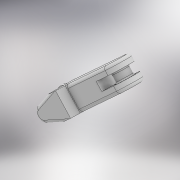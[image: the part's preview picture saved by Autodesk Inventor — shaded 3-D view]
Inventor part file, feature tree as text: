
AUTODESK INVENTOR PART (.ipt)
format: ipt  version: 2022 (Build 260153000, 153)  size: 250,368 bytes
history: native  units: mm
features: extrude x7, sketch x6, fillet x3, chamfer x2, plane x1, projected_geometry x1
ambient origin geometry x8: Origin, YZ Plane, XZ Plane, XY Plane, X Axis, Y Axis, Z Axis, Center Point
bodies: Solid1 (feature_tree)
feature tree (20):
  sketch  "Sketch1"  dims[d1=2.5mm d3=1.5mm]
  extrude  "Extrusion1"  Depth=2.5mm
  extrude  "Extrusion2"  Depth=7.0mm
  extrude  "Extrusion3"  Depth=35.0mm
  extrude  "Extrusion4"  Depth=10.0mm TaperAngle=0.0deg
  extrude  "Extrusion5"  Depth=18.0mm
  extrude  "Extrusion6"  Depth=0.5mm TaperAngle=0.0deg
  chamfer  "Chamfer1"  Distance=35.25mm
  fillet  "Fillet1"  Radius=7.0mm
  extrude  "Extrusion7"  Depth=0.5mm
  plane  "Work Plane1"
  fillet  "Fillet2"  Radius=1.2mm
  chamfer  "Chamfer2"  Distance=2.0mm Angle=45.0deg
  fillet  "Fillet3"  Radius=1.0mm
  sketch  "Sketch2"  dims[d4=5.0mm d6=7.0mm]
  projected_geometry  "Projected Loop1"
  sketch  "Sketch3"  dims[d7=1.0mm d8=35.0mm]
  sketch  "Sketch4"  dims[d9=10.0mm d10=8.5mm d11=0.0mm]
  sketch  "Sketch5"  dims[d12=12.5mm d13=0.0mm d14=18.0mm]
  sketch  "Sketch6"  dims[d15=2.5mm d16=12.5mm d17=0.0mm d18=35.25mm d19=0.0mm d20=7.0mm d21=0.0mm d22=8.1mm d23=1.2mm d24=0.0mm d25=2.0mm d26=2.0mm d27=45.0deg d28=1.0mm d29=5.0mm d30=1.2mm d31=0.0mm d32=0.5mm d33=1.0mm d34=2.0mm d35=45.0deg d36=0.5mm]
